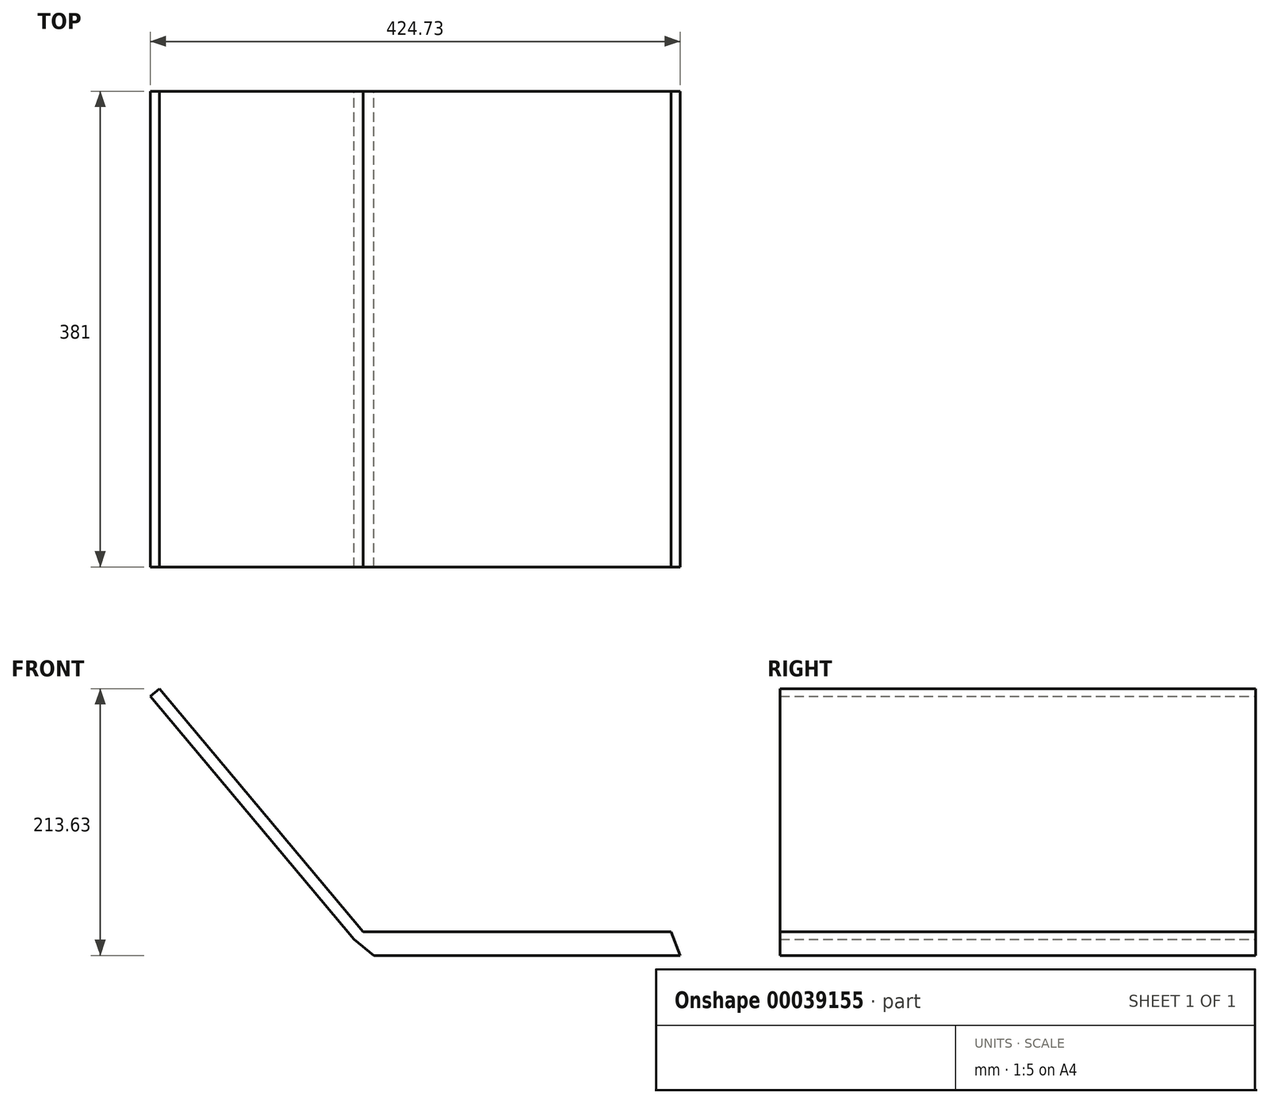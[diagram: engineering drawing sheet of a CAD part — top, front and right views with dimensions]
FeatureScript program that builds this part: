
annotation { "Feature Type Name" : "Feature", "Feature Type Description" : "" }
export const myFeature = defineFeature(function(context is Context, id is Id, definition is map)
    precondition{}
    {
        {
            var Q0;
            Q0=qCreatedBy(makeId("Front.planeOp"),FACE);
            var sketch = newSketch(context, id + "F0", { "sketchPlane" : qUnion([Q0])});
            skLineSegment(sketch, "E0", {"start": v(122.8, 0) * mm, "end": v(-122.8, 0) * mm});
            skLineSegment(sketch, "E1", {"start": v(-122.8, 0) * mm, "end": v(-138.66, 12.93) * mm});
            skLineSegment(sketch, "E2", {"start": v(-138.66, 12.93) * mm, "end": v(-301.93, 207.5) * mm});
            skLineSegment(sketch, "E3", {"start": v(-301.93, 207.5) * mm, "end": v(-294.63, 213.63) * mm});
            skLineSegment(sketch, "E4", {"start": v(-294.63, 213.63) * mm, "end": v(-131.37, 19.05) * mm});
            skLineSegment(sketch, "E5", {"start": v(-131.37, 19.05) * mm, "end": v(115.34, 19.05) * mm});
            skLineSegment(sketch, "E6", {"start": v(115.34, 19.05) * mm, "end": v(122.8, 0) * mm});
            skSolve(sketch);
        }
        {
            var Q0;
            Q0 = qSketchRegion(id + "F0", true);
            extrude(context, id + "F1", {"entities" : qUnion([Q0]), "endBound" : BoundingType.SYMMETRIC, "depth" : 381 * mm});
        }
    });
